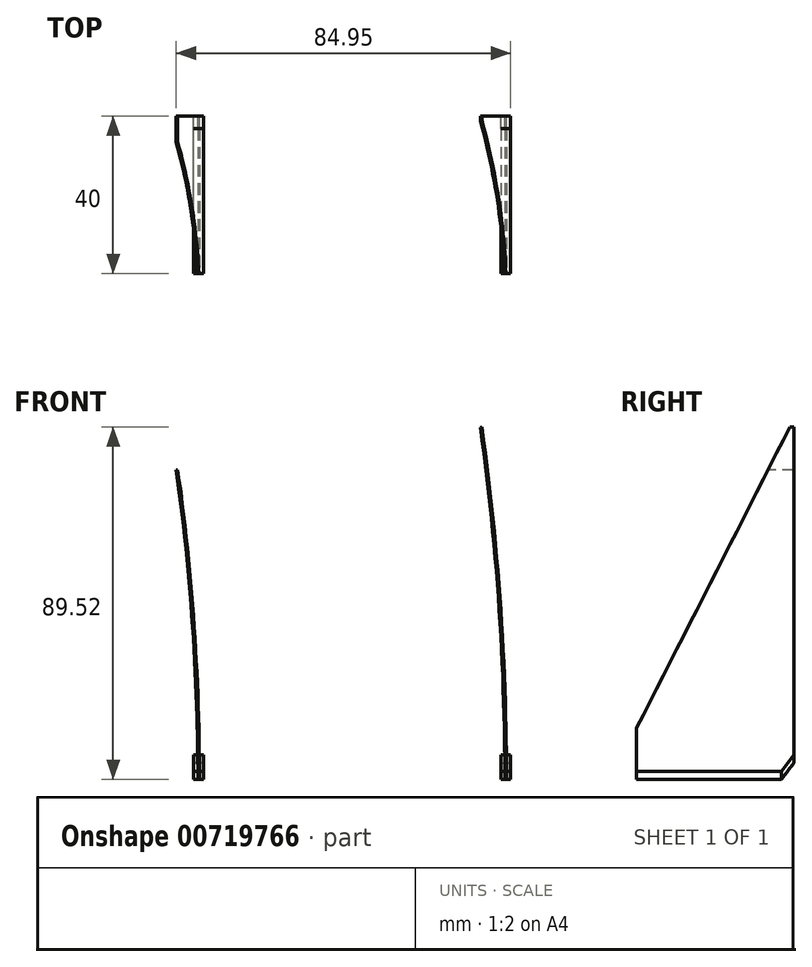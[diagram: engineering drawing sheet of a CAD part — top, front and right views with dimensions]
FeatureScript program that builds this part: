
annotation { "Feature Type Name" : "Feature", "Feature Type Description" : "" }
export const myFeature = defineFeature(function(context is Context, id is Id, definition is map)
    precondition{}
    {
        {
            var Q0;
            Q0=qCreatedBy(makeId("Top.planeOp"),FACE);
            var sketch = newSketch(context, id + "F0", { "sketchPlane" : qUnion([Q0])});
            skLineSegment(sketch, "E0.bottom", {"start": v(38.8, 0) * mm, "end": v(39.2, 0) * mm});
            skLineSegment(sketch, "E0.top", {"start": v(38.8, -40) * mm, "end": v(39.2, -40) * mm});
            skLineSegment(sketch, "E0.left", {"start": v(38.8, 0) * mm, "end": v(38.8, -40) * mm});
            skLineSegment(sketch, "E0.right", {"start": v(39.2, 0) * mm, "end": v(39.2, -40) * mm});
            skLineSegment(sketch, "E1.bottom", {"start": v(116.8, 0) * mm, "end": v(117.2, 0) * mm});
            skLineSegment(sketch, "E1.top", {"start": v(116.8, -40) * mm, "end": v(117.2, -40) * mm});
            skLineSegment(sketch, "E1.left", {"start": v(116.8, 0) * mm, "end": v(116.8, -40) * mm});
            skLineSegment(sketch, "E1.right", {"start": v(117.2, 0) * mm, "end": v(117.2, -40) * mm});
            skLineSegment(sketch, "E2", {"start": v(-526, 0) * mm, "end": v(-526, -99.21) * mm});
            skSolve(sketch);
        }
        {
            var Q0;
            Q0=makeQuery(id+"F0.imprint","IMPRINT",FACE,{"disambiguationData":[TD([[makeQuery(id+"F0.imprint","IMPRINT",EDGE,{"derivedFrom":sQuery(id+"F0.wireOp",EDGE,"E0.bottom")}),-1.0]])]});
            var Q1;
            Q1=makeQuery(id+"F0.imprint","IMPRINT",FACE,{"disambiguationData":[TD([[makeQuery(id+"F0.imprint","IMPRINT",EDGE,{"derivedFrom":sQuery(id+"F0.wireOp",EDGE,"E1.bottom")}),-1.0]])]});
            var Q2;
            Q2=sQuery(id+"F0.wireOp",EDGE,"E2");
            revolve(context, id + "F1", {"surfaceOperationType" : NewSurfaceOperationType.NEW, "entities" : qUnion([Q0, Q1]), "axis" : qUnion([Q2]), "revolveType" : RevolveType.ONE_DIRECTION, "angle" : 8 * degree});
        }
        {
            var Q0;
            Q0=qCreatedBy(makeId("Right.planeOp"),FACE);
            var sketch = newSketch(context, id + "F2", { "sketchPlane" : qUnion([Q0])});
            skLineSegment(sketch, "E3", {"start": v(3.72, 98.87) * mm, "end": v(-49.53, -5.68) * mm});
            skLineSegment(sketch, "E4", {"start": v(-49.53, -5.68) * mm, "end": v(-7.54, -5.68) * mm});
            skLineSegment(sketch, "E5", {"start": v(-7.54, -5.68) * mm, "end": v(3.5, 8.82) * mm});
            skLineSegment(sketch, "E6", {"start": v(3.5, 8.82) * mm, "end": v(3.5, -12.39) * mm});
            skLineSegment(sketch, "E7", {"start": v(3.5, -12.39) * mm, "end": v(-69.23, -12.39) * mm});
            skLineSegment(sketch, "E8", {"start": v(-69.23, -12.39) * mm, "end": v(-69.23, 98.87) * mm});
            skLineSegment(sketch, "E9", {"start": v(-69.23, 98.87) * mm, "end": v(3.72, 98.87) * mm});
            skSolve(sketch);
        }
        {
            var Q0;
            Q0=makeQuery(id+"F2.imprint","IMPRINT",FACE,{"disambiguationData":[TD([[makeQuery(id+"F2.imprint","IMPRINT",EDGE,{"derivedFrom":sQuery(id+"F2.wireOp",EDGE,"E3")}),-1.0]])]});
            extrude(context, id + "F3", {"entities" : qUnion([Q0]), "operationType" : NewBodyOperationType.REMOVE, "depth" : 162 * mm, "offsetDistance" : 25 * mm});
        }
        {
            var Q0;
            Q0=makeQuery(id+"F1.opRevolve","CAP_FACE",FACE,{"disambiguationData":[OSD([sQuery(id+"F0.wireOp",EDGE,"E1.bottom"),sQuery(id+"F0.wireOp",EDGE,"E1.top"),sQuery(id+"F0.wireOp",EDGE,"E1.left"),sQuery(id+"F0.wireOp",EDGE,"E1.right")])],"isStart":true});
            var sketch = newSketch(context, id + "F4", { "sketchPlane" : qUnion([Q0])});
            skLineSegment(sketch, "E10.bottom", {"start": v(118.25, 3.21) * mm, "end": v(115.75, 3.21) * mm});
            skLineSegment(sketch, "E10.top", {"start": v(118.25, 40) * mm, "end": v(115.75, 40) * mm});
            skLineSegment(sketch, "E10.left", {"start": v(118.25, 3.21) * mm, "end": v(118.25, 40) * mm});
            skLineSegment(sketch, "E10.right", {"start": v(115.75, 3.21) * mm, "end": v(115.75, 40) * mm});
            skLineSegment(sketch, "E11.bottom", {"start": v(40.25, 40) * mm, "end": v(37.75, 40) * mm});
            skLineSegment(sketch, "E11.top", {"start": v(40.25, 3.21) * mm, "end": v(37.75, 3.21) * mm});
            skLineSegment(sketch, "E11.left", {"start": v(40.25, 40) * mm, "end": v(40.25, 3.21) * mm});
            skLineSegment(sketch, "E11.right", {"start": v(37.75, 40) * mm, "end": v(37.75, 3.21) * mm});
            skSolve(sketch);
        }
        {
            var Q0;
            {var subQ2=sQuery(id+"F4.wireOp",EDGE,"E10.right");Q0=makeQuery(id+"F4.imprint","IMPRINT",FACE,{"disambiguationData":[TD([[makeQuery(id+"F4.imprint","IMPRINT",EDGE,{"derivedFrom":subQ2}),-1.0]])]});}
            var Q1;
            {var subQ2=sQuery(id+"F4.wireOp",EDGE,"E10.left");Q1=makeQuery(id+"F4.imprint","IMPRINT",FACE,{"disambiguationData":[TD([[makeQuery(id+"F4.imprint","IMPRINT",EDGE,{"derivedFrom":subQ2}),1.0]])]});}
            var Q2;
            {var subQ1=makeQuery(id+"F1.opRevolve","CAP_EDGE",EDGE,{"disambiguationData":[OSD([sQuery(id+"F0.wireOp",EDGE,"E1.left")])],"isStart":true});Q2=makeQuery(id+"F4.imprint","IMPRINT",FACE,{"disambiguationData":[TD([[makeQuery(id+"F4.imprint","IMPRINT",EDGE,{"derivedFrom":subQ1}),-1.0]])]});}
            var Q3;
            Q3=makeQuery(id+"F4.imprint","IMPRINT",FACE,{"disambiguationData":[TD([[makeQuery(id+"F4.imprint","IMPRINT",EDGE,{"derivedFrom":sQuery(id+"F4.wireOp",EDGE,"E11.bottom")}),1.0]])]});
            extrude(context, id + "F5", {"entities" : qUnion([Q0, Q1, Q2, Q3]), "oppositeDirection" : true, "depth" : 2 * mm, "offsetDistance" : 25 * mm});
        }
        {
            var Q0;
            Q0=makeQuery(id+"F5.opExtrude","SWEPT_FACE",FACE,{"disambiguationData":[OSD([sQuery(id+"F4.wireOp",EDGE,"E10.left")])]});
            var sketch = newSketch(context, id + "F6", { "sketchPlane" : qUnion([Q0])});
            skLineSegment(sketch, "E12", {"start": v(-3.21, 2) * mm, "end": v(0, 6.24) * mm});
            skLineSegment(sketch, "E13", {"start": v(0, 6.24) * mm, "end": v(0, 4.23) * mm});
            skLineSegment(sketch, "E14", {"start": v(0, 4.23) * mm, "end": v(-3.21, 0) * mm});
            skLineSegment(sketch, "E15", {"start": v(-3.21, 0) * mm, "end": v(-3.21, 2) * mm});
            skSolve(sketch);
        }
        {
            var Q0;
            Q0=makeQuery(id+"F6.imprint","IMPRINT",FACE,{"disambiguationData":[TD([[makeQuery(id+"F6.imprint","IMPRINT",EDGE,{"derivedFrom":sQuery(id+"F6.wireOp",EDGE,"E12")}),-1.0]])]});
            extrude(context, id + "F7", {"entities" : qUnion([Q0]), "oppositeDirection" : true, "depth" : 2.5 * mm, "offsetDistance" : 25 * mm});
        }
        {
            var Q0;
            Q0=makeQuery(id+"F5.opExtrude","SWEPT_FACE",FACE,{"disambiguationData":[OSD([sQuery(id+"F4.wireOp",EDGE,"E11.right")])]});
            var sketch = newSketch(context, id + "F8", { "sketchPlane" : qUnion([Q0])});
            skLineSegment(sketch, "E16", {"start": v(3.21, 2) * mm, "end": v(0, 6.2) * mm});
            skLineSegment(sketch, "E17", {"start": v(0, 6.2) * mm, "end": v(0, 4.25) * mm});
            skLineSegment(sketch, "E18", {"start": v(0, 4.25) * mm, "end": v(3.21, 0) * mm});
            skLineSegment(sketch, "E19", {"start": v(3.21, 0) * mm, "end": v(3.21, 2) * mm});
            skSolve(sketch);
        }
        {
            var Q0;
            Q0=makeQuery(id+"F8.imprint","IMPRINT",FACE,{"disambiguationData":[TD([[makeQuery(id+"F8.imprint","IMPRINT",EDGE,{"derivedFrom":sQuery(id+"F8.wireOp",EDGE,"E16")}),1.0]])]});
            extrude(context, id + "F9", {"entities" : qUnion([Q0]), "oppositeDirection" : true, "depth" : 2.5 * mm, "offsetDistance" : 25 * mm});
        }
    });
